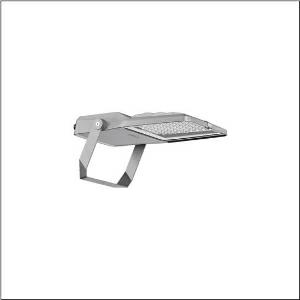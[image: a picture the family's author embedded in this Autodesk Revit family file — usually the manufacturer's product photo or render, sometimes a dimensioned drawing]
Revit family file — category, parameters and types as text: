
# Revit family: floodlight_fl_21_mini___rs12_5xa7772b3b1a_ddef
name_source: partatom
category: Lighting Fixtures
units: mm (PartAtom-declared; Revit-internal decimal feet)

## family parameters
Cut with Voids When Loaded = No
Host = Face
Light Source = No
Part Type = Normal
Room Calculation Point = No
Round Connector Dimension = Use Diameter
Shared = No

## types (1)
- --- (1 x LED, 5430 lm, 45.5 W, 3000K)
    Apparent Load = 46 VA
    CIE Flux Codes = 79 92 99 100 100
    Color Rendering = 80
    Color Temperature = 3000K
    Default Elevation = 1800 mm
    Description = Floodlight FL 21 mini, floodlight, primary light control with lens, of PMMA, primary optical cover: protective disc, of toughened safety glass, transparent, light distribution: RS12, light emission: direct distribution, installation type: surface-mounted, LED, High Power LED, rated luminous flux: 5.430lm, luminous efficacy: 119lm/W, light colour: 830, colour temperature: 3000K, control gear: ECG iQ, control: Street-Remote, Auto-Match, Temp-Guard, Night-Set, Smart-Wire, Desk-Remote (wireless, voltage-free reading and setting of iQ features in the workshop via application-optimized NFC function/RFID function), optimised constant luminous flux control (CLO 2.0), with terminal, 6-pole, mains connection: 220..240V, AC, 50/60Hz, start of lifetime: 46W, end of lifetime: 48W, reduction: 21W, luminaire housing, of diecast aluminium, powder-coated, Siteco® metallic grey (DB 702S), corrosivity category C5 according to DIN EN ISO 12944, mounting bracket, of steel, galvanised, powder-coated, Siteco® metallic grey (DB 702S), protection rating (complete): IP66, insulation class (complete): insulation class II (safety insulation), certification: CE, ENEC, VDE, protection symbol: D, impact resistance: IK08, permissible operating ambient temperature: -40..+40°C, permissible operating ambient temperature for outdoor applications: -40..+50°C, standard: DIN EN 12944, packaging unit: 1 piece

Light Distribution: RS12
    Height = 70 mm
    Lamp = 1 x LED
    Lamp Light Flux = 5430 lm
    Lamp Power = 45.5 W
    Lamp count = 1
    Length = 485 mm
    Luminous efficacy = 119 lm/W
    Manufacturer = Siteco
    ModVariant = No
    Model = 5XA7772B3B1A
    Number of Poles = 1
    OnlyDefault = Yes
    Power Factor = 1
    Product Name = Floodlight FL 21 mini | RS12
    Product group = floodlight | pylon top
    ProductGroupID = 6101
    Protection Class = Protection class II
    Protection Degree = IP 66
    RLX_Detail_Level = 1
    RlxData = <blob elided: 90673 chars, md5=3e5602fb>
    Socket = socket
    Standby Power = 0 W
    System Light Flux = 5430 lm
    System Power = 46 W
    Type Comments = factory setting: luminous flux: 100 % | dim-lin: 254 | 463 mA
    Type Image = l_1006845.jpg
    URL = http://relux.com
    VarID = @adj_078919
    Voltage = 0 V
    Weight = 0.00 kg
    Width = 337 mm

## geometry (parser evidence)
native form markers: Blend x4, Sweep x14
no freeform markers — native parametric forms only
